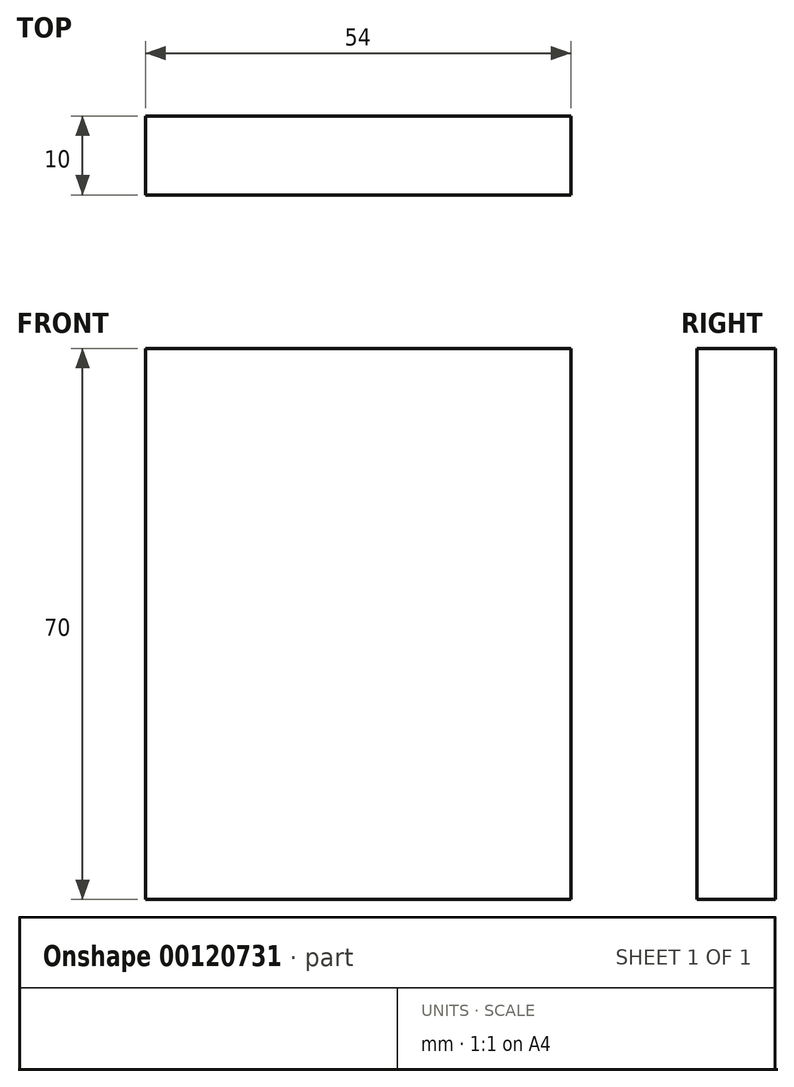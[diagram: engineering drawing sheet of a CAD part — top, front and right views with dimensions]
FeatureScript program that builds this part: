
annotation { "Feature Type Name" : "Feature", "Feature Type Description" : "" }
export const myFeature = defineFeature(function(context is Context, id is Id, definition is map)
    precondition{}
    {
        {
            var Q0;
            Q0=qCreatedBy(makeId("Front.planeOp"),FACE);
            var sketch = newSketch(context, id + "F0", { "sketchPlane" : qUnion([Q0])});
            skLineSegment(sketch, "E0.bottom", {"start": v(-28.02, 43.4) * mm, "end": v(25.98, 43.4) * mm});
            skLineSegment(sketch, "E0.top", {"start": v(-28.02, -26.6) * mm, "end": v(25.98, -26.6) * mm});
            skLineSegment(sketch, "E0.left", {"start": v(-28.02, 43.4) * mm, "end": v(-28.02, -26.6) * mm});
            skLineSegment(sketch, "E0.right", {"start": v(25.98, 43.4) * mm, "end": v(25.98, -26.6) * mm});
            skSolve(sketch);
        }
        {
            var Q0;
            Q0=makeQuery(id+"F0.imprint","IMPRINT",FACE,{"disambiguationData":[TD([[makeQuery(id+"F0.imprint","IMPRINT",EDGE,{"derivedFrom":sQuery(id+"F0.wireOp",EDGE,"E0.bottom")}),-1.0]])]});
            extrude(context, id + "F1", {"entities" : qUnion([Q0]), "depth" : 10 * mm});
        }
    });
